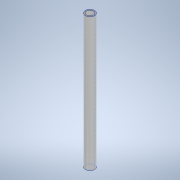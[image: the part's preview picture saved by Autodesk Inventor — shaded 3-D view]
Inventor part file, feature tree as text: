
AUTODESK INVENTOR PART (.ipt)
format: ipt  version: 2020.3 (Build 243373000, 373)  size: 98,304 bytes
history: native  units: mm
features: sketch x2, other x1, extrude x1, hole x1
ambient origin geometry x8: Origin, YZ Plane, XZ Plane, XY Plane, X Axis, Y Axis, Z Axis, Center Point
bodies: Body1 (feature_tree)
feature tree (5):
  other  "ソリッド1"
  extrude  "押し出し1"  Depth=4.0mm
  hole  "穴1"  [1 undecoded]
  sketch  "スケッチ1"
  sketch  "スケッチ2"
note: 1 required parameter value undecoded (feature->parameter linkage not recoverable at this tier; creation-order binding heuristic only, values carry confidence <= 0.55)
